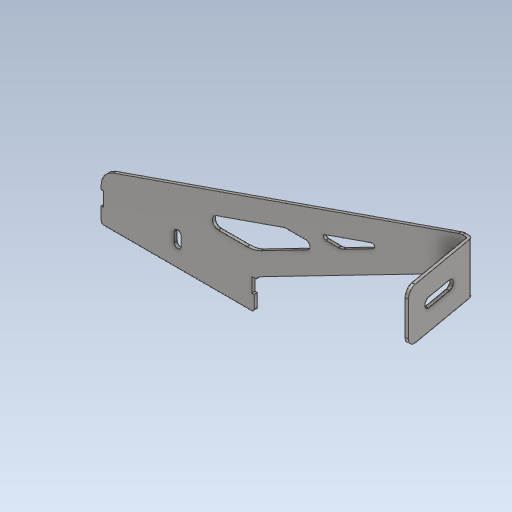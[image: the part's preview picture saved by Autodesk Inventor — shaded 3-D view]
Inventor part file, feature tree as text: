
AUTODESK INVENTOR PART (.ipt)
format: ipt  version: 2020 (Build 240168000, 168)  size: 202,752 bytes
history: native  units: mm
features: other x4, sketch x1, plane x1
ambient origin geometry x8: Origin, YZ Plane, XZ Plane, XY Plane, X Axis, Y Axis, Z Axis, Center Point
bodies: Body1 (feature_tree)
feature tree (6):
  other  "吊架-長(R)(#11.02).ipt"
  other  "實體1::吊架-長(R)(#11.02).ipt"
  other  "標籤特徵1"
  sketch  "草圖1"
  plane  "工作平面1"
  other  "實體1"
